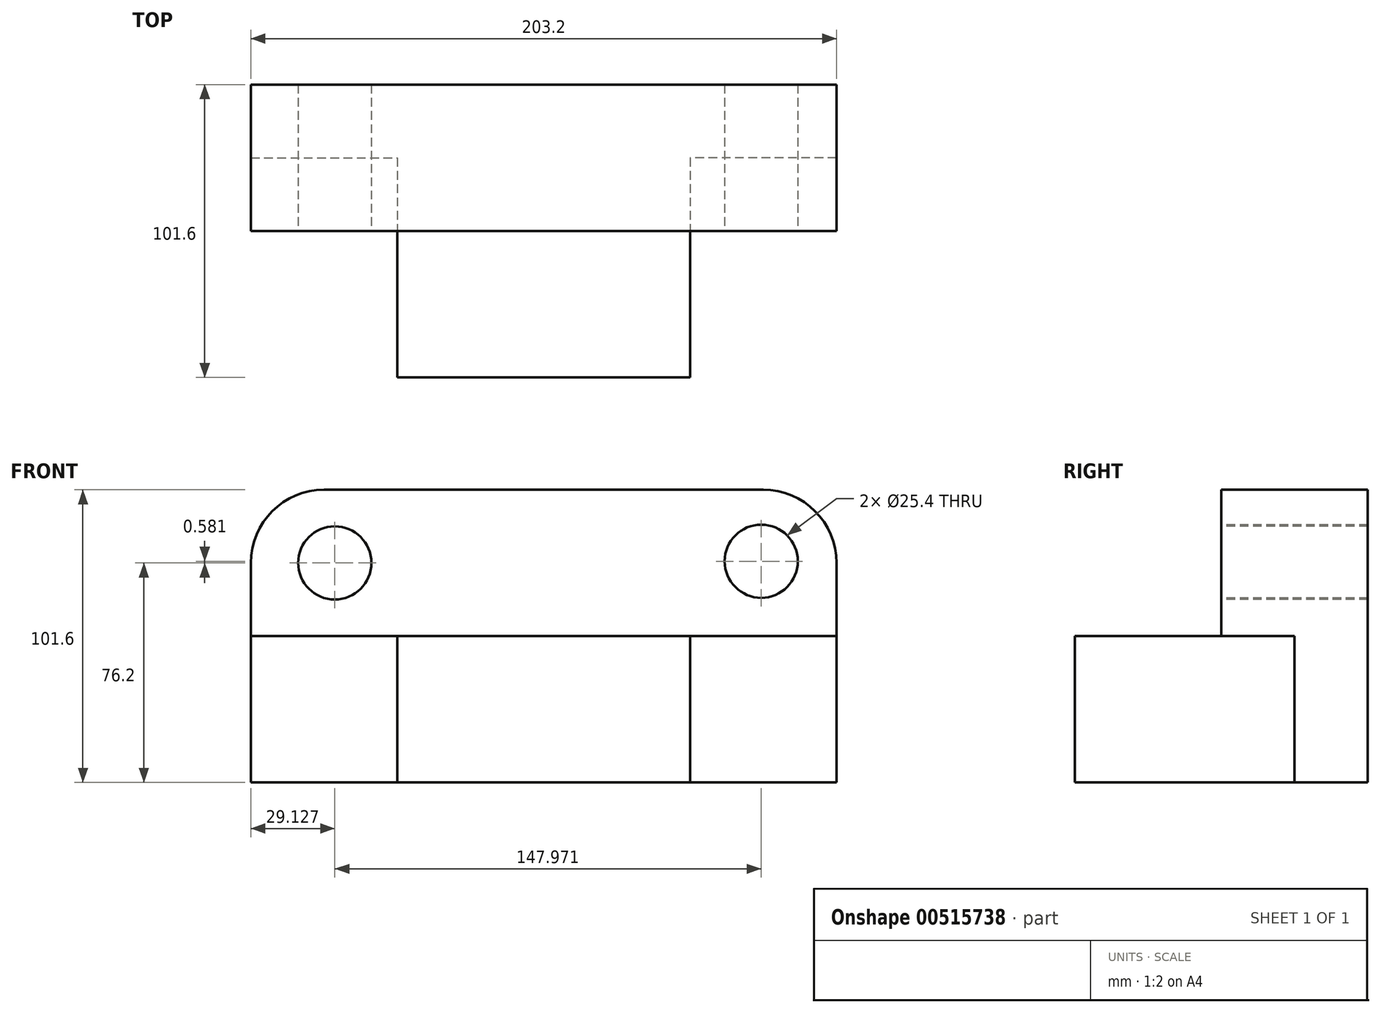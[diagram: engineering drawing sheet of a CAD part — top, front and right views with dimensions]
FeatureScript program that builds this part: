
annotation { "Feature Type Name" : "Feature", "Feature Type Description" : "" }
export const myFeature = defineFeature(function(context is Context, id is Id, definition is map)
    precondition{}
    {
        {
            var Q0;
            Q0=qCreatedBy(makeId("Top.planeOp"),FACE);
            var sketch = newSketch(context, id + "F0", { "sketchPlane" : qUnion([Q0])});
            skLineSegment(sketch, "E0.bottom", {"start": v(-95.23, 33.66) * mm, "end": v(107.97, 33.66) * mm});
            skLineSegment(sketch, "E0.top", {"start": v(-95.23, -67.94) * mm, "end": v(107.97, -67.94) * mm});
            skLineSegment(sketch, "E0.left", {"start": v(-95.23, 33.66) * mm, "end": v(-95.23, -67.94) * mm});
            skLineSegment(sketch, "E0.right", {"start": v(107.97, 33.66) * mm, "end": v(107.97, -67.94) * mm});
            skSolve(sketch);
        }
        {
            var Q0;
            Q0 = qSketchRegion(id + "F0", true);
            extrude(context, id + "F1", {"entities" : qUnion([Q0]), "depth" : 101.6 * mm, "offsetDistance" : 25.4 * mm});
        }
        {
            var Q0;
            Q0=makeQuery(id+"F1.opExtrude","SWEPT_FACE",FACE,{"disambiguationData":[OSD([sQuery(id+"F0.wireOp",EDGE,"E0.top")])]});
            var sketch = newSketch(context, id + "F2", { "sketchPlane" : qUnion([Q0])});
            skLineSegment(sketch, "E1.bottom", {"start": v(-95.23, 0) * mm, "end": v(-44.43, 0) * mm});
            skLineSegment(sketch, "E1.top", {"start": v(-95.23, 50.8) * mm, "end": v(-44.43, 50.8) * mm});
            skLineSegment(sketch, "E1.left", {"start": v(-95.23, 0) * mm, "end": v(-95.23, 50.8) * mm});
            skLineSegment(sketch, "E1.right", {"start": v(-44.43, 0) * mm, "end": v(-44.43, 50.8) * mm});
            skLineSegment(sketch, "E2.bottom", {"start": v(107.97, 0) * mm, "end": v(57.17, 0) * mm});
            skLineSegment(sketch, "E2.top", {"start": v(107.97, 50.8) * mm, "end": v(57.17, 50.8) * mm});
            skLineSegment(sketch, "E2.left", {"start": v(107.97, 0) * mm, "end": v(107.97, 50.8) * mm});
            skLineSegment(sketch, "E2.right", {"start": v(57.17, 0) * mm, "end": v(57.17, 50.8) * mm});
            skSolve(sketch);
        }
        {
            var Q0;
            Q0=makeQuery(id+"F2.imprint","IMPRINT",FACE,{"disambiguationData":[TD([[makeQuery(id+"F2.imprint","IMPRINT",EDGE,{"derivedFrom":sQuery(id+"F2.wireOp",EDGE,"E1.bottom")}),1.0]])]});
            var Q1;
            Q1=makeQuery(id+"F2.imprint","IMPRINT",FACE,{"disambiguationData":[TD([[makeQuery(id+"F2.imprint","IMPRINT",EDGE,{"derivedFrom":sQuery(id+"F2.wireOp",EDGE,"E2.bottom")}),1.0]])]});
            extrude(context, id + "F3", {"entities" : qUnion([Q0, Q1]), "operationType" : NewBodyOperationType.REMOVE, "oppositeDirection" : true, "depth" : 76.2 * mm, "offsetDistance" : 25.4 * mm});
        }
        {
            var Q0;
            Q0=makeQuery(id+"F1.opExtrude","SWEPT_FACE",FACE,{"disambiguationData":[OSD([sQuery(id+"F0.wireOp",EDGE,"E0.top")])]});
            var sketch = newSketch(context, id + "F4", { "sketchPlane" : qUnion([Q0])});
            skLineSegment(sketch, "E3.bottom", {"start": v(-95.23, 50.8) * mm, "end": v(107.97, 50.8) * mm});
            skLineSegment(sketch, "E3.top", {"start": v(-95.23, 101.6) * mm, "end": v(107.97, 101.6) * mm});
            skLineSegment(sketch, "E3.left", {"start": v(-95.23, 50.8) * mm, "end": v(-95.23, 101.6) * mm});
            skLineSegment(sketch, "E3.right", {"start": v(107.97, 50.8) * mm, "end": v(107.97, 101.6) * mm});
            skSolve(sketch);
        }
        {
            var Q0;
            Q0 = qSketchRegion(id + "F4", true);
            extrude(context, id + "F5", {"entities" : qUnion([Q0]), "operationType" : NewBodyOperationType.REMOVE, "oppositeDirection" : true, "depth" : 50.8 * mm, "offsetDistance" : 25.4 * mm});
        }
        {
            var Q0;
            Q0=makeQuery(id+"F1.opExtrude","CAP_EDGE",EDGE,{"disambiguationData":[OSD([sQuery(id+"F0.wireOp",EDGE,"E0.right")])],"isStart":false});
            var Q1;
            Q1=makeQuery(id+"F1.opExtrude","CAP_EDGE",EDGE,{"disambiguationData":[OSD([sQuery(id+"F0.wireOp",EDGE,"E0.left")])],"isStart":false});
            fillet(context, id + "F6", {"entities" : qUnion([Q0, Q1]), "radius" : 25.4 * mm, "tangentPropagation" : true, "allowEdgeOverflow" : false});
        }
        {
            var Q0;
            Q0=makeQuery(id+"F5.boolean.opBoolean","COPY",FACE,{"derivedFrom":makeQuery(id+"F5.opExtrude","CAP_FACE",FACE,{"disambiguationData":[OSD([sQuery(id+"F4.wireOp",EDGE,"E3.bottom"),sQuery(id+"F4.wireOp",EDGE,"E3.top"),sQuery(id+"F4.wireOp",EDGE,"E3.left"),sQuery(id+"F4.wireOp",EDGE,"E3.right")])],"isStart":false})});
            var sketch = newSketch(context, id + "F7", { "sketchPlane" : qUnion([Q0])});
            skCircle(sketch, "E4", {"center": v(81.87, 76.78) * mm, "radius": 12.7 * mm});
            skCircle(sketch, "E5", {"center": v(-66.1, 76.2) * mm, "radius": 12.7 * mm});
            skSolve(sketch);
        }
        {
            var Q0;
            Q0=makeQuery(id+"F7.imprint","IMPRINT",FACE,{"disambiguationData":[TD([[makeQuery(id+"F7.imprint","IMPRINT",EDGE,{"derivedFrom":sQuery(id+"F7.wireOp",EDGE,"E4")}),1.0]])]});
            var Q1;
            Q1=makeQuery(id+"F7.imprint","IMPRINT",FACE,{"disambiguationData":[TD([[makeQuery(id+"F7.imprint","IMPRINT",EDGE,{"derivedFrom":sQuery(id+"F7.wireOp",EDGE,"E5")}),1.0]])]});
            extrude(context, id + "F8", {"entities" : qUnion([Q0, Q1]), "operationType" : NewBodyOperationType.REMOVE, "oppositeDirection" : true, "depth" : 101.6 * mm, "offsetDistance" : 25.4 * mm});
        }
    });
